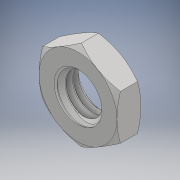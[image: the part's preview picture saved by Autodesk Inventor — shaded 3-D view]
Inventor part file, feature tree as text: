
AUTODESK INVENTOR PART (.ipt)
format: ipt  version: 2018 (Build 220112000, 112)  size: 289,792 bytes
history: native  units: mm
features: other x1, mirror x1
ambient origin geometry x8: Origin, YZ Plane, XZ Plane, XY Plane, X Axis, Y Axis, Z Axis, Center Point
bodies: Body1 (feature_tree)
feature tree (2):
  other  "Sólido1"
  mirror  "Mirror1"
